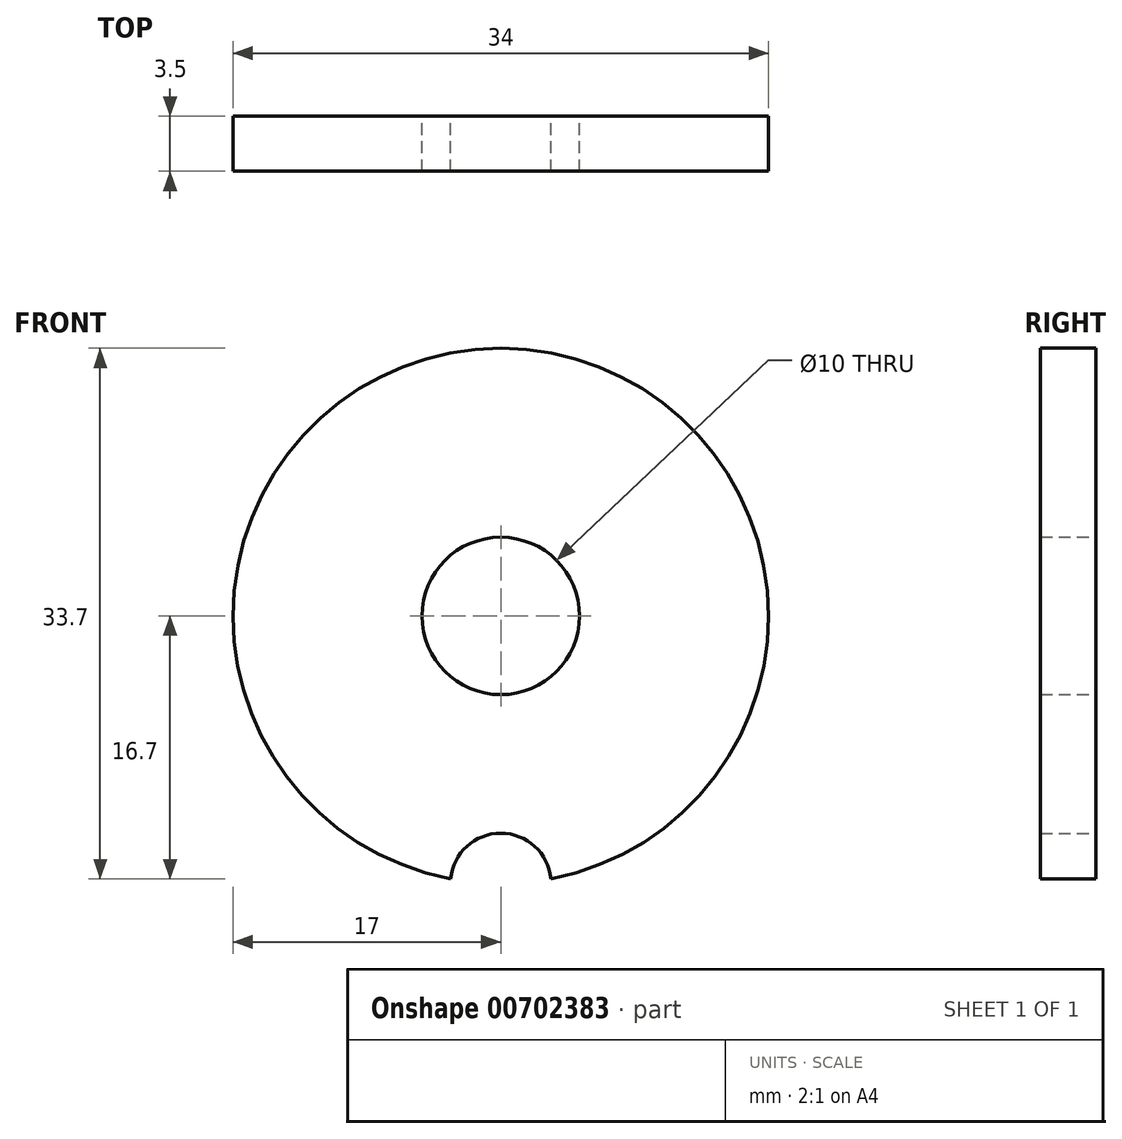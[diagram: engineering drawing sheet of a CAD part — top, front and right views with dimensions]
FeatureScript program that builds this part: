
annotation { "Feature Type Name" : "Feature", "Feature Type Description" : "" }
export const myFeature = defineFeature(function(context is Context, id is Id, definition is map)
    precondition{}
    {
        {
            var Q0;
            Q0=qCreatedBy(makeId("Front.planeOp"),FACE);
            var sketch = newSketch(context, id + "F0", { "sketchPlane" : qUnion([Q0])});
            skCircle(sketch, "E0", {"center": v(0, 0) * mm, "radius": 5 * mm});
            skArc(sketch, "E1", {"start": v(3.19, -16.7) * mm, "mid": v(0, 17) * mm, "end": v(-3.19, -16.7) * mm});
            skArc(sketch, "E2", {"start": v(3.19, -16.7) * mm, "mid": v(0, -13.8) * mm, "end": v(-3.19, -16.7) * mm});
            skSolve(sketch);
        }
        {
            var Q0;
            Q0 = qSketchRegion(id + "F0", true);
            extrude(context, id + "F1", {"entities" : qUnion([Q0]), "depth" : 3.5 * mm, "offsetDistance" : 25 * mm});
        }
    });
